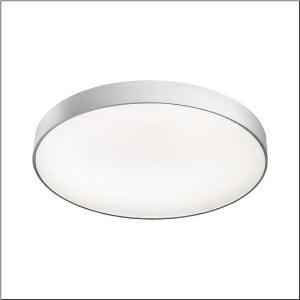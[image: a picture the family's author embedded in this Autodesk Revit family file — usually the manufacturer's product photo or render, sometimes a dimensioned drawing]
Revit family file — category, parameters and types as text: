
# Revit family: round_21_l_51mr38nd0421s
name_source: partatom
category: Lighting Fixtures
units: mm (PartAtom-declared; Revit-internal decimal feet)

## family parameters
Cut with Voids When Loaded = No
Host = Face
Light Source = No
Part Type = Normal
Room Calculation Point = No
Round Connector Dimension = Use Diameter
Shared = No

## types (1)
- Round 21 L (1 x LED, 12230 lm, 88.2 W, 4000K)
    Apparent Load = 88 VA
    CIE Flux Codes = 66 90 98 71 100
    Color Rendering = 80
    Color Temperature = 4000K
    Default Elevation = 1800 mm
    Description = Round 21 L, wall and ceiling luminaire, primary optical cover: micro prismatic cover, of PMMA, transparent, CAT 2 (L<= 3000cd/m²), light emission: direct/indirect distribution, primary light characteristic: symmetric, installation type: suspended mounting, surface-mounted, LED, rated luminous flux: 12.230lm, luminous efficacy: 139lm/W, light colour: 840, colour temperature: 4000K, with terminal, 5-pole, mains connection: 230V, AC, 50/60Hz, rated input power: 88W, housing, of aluminium, coated, silver, diameter: 850mm, height: 62mm, protection rating (complete): IP40, insulation class (complete): insulation class I (protective earthing), certification: CE, impact resistance: IK04, permissible operating ambient temperature: -10..+35°C, packaging unit: 1 piece
    Height = 87 mm
    Lamp = 1 x LED
    Lamp Light Flux = 12230 lm
    Lamp Power = 88.2 W
    Lamp count = 1
    Length = 850 mm
    Luminous efficacy = 139 lm/W
    Manufacturer = Siteco
    ModVariant = No
    Model = 51MR38ND0421S
    Mounting Place = Ceiling
    Mounting Type = Surface mounted
    Number of Poles = 1
    OnlyDefault = Yes
    Power Factor = 1
    Product Name = Round 21 L
    Product group = wall and ceiling luminaire
    ProductGroupID = 303
    Protection Class = Protection class I
    Protection Degree = IP 40
    RLX_Detail_Level = 1
    RLX_Emergency_Light_Flux = 0 lm
    RLX_Emergency_Type = 0
    RLX_Emergency_Type_DB = No
    RlxData = <blob elided: 25161 chars, md5=7f1d0ced>
    Socket = socket
    Standby Power = 0 W
    System Light Flux = 12230 lm
    System Power = 88 W
    Type Comments = Product without accessories
    Type Image = l_1258322.jpg
    URL = http://relux.com
    VarID = ---
    Voltage = 0 V
    Weight = 0.00 kg
    Width = 0 mm  [stored 0 ft]

note: [stored X ft] marks values corroborated as IEEE doubles in the binary element streams (Revit-internal decimal feet)

## geometry (parser evidence)
native form markers: Blend x4, Sweep x14
no freeform markers — native parametric forms only
